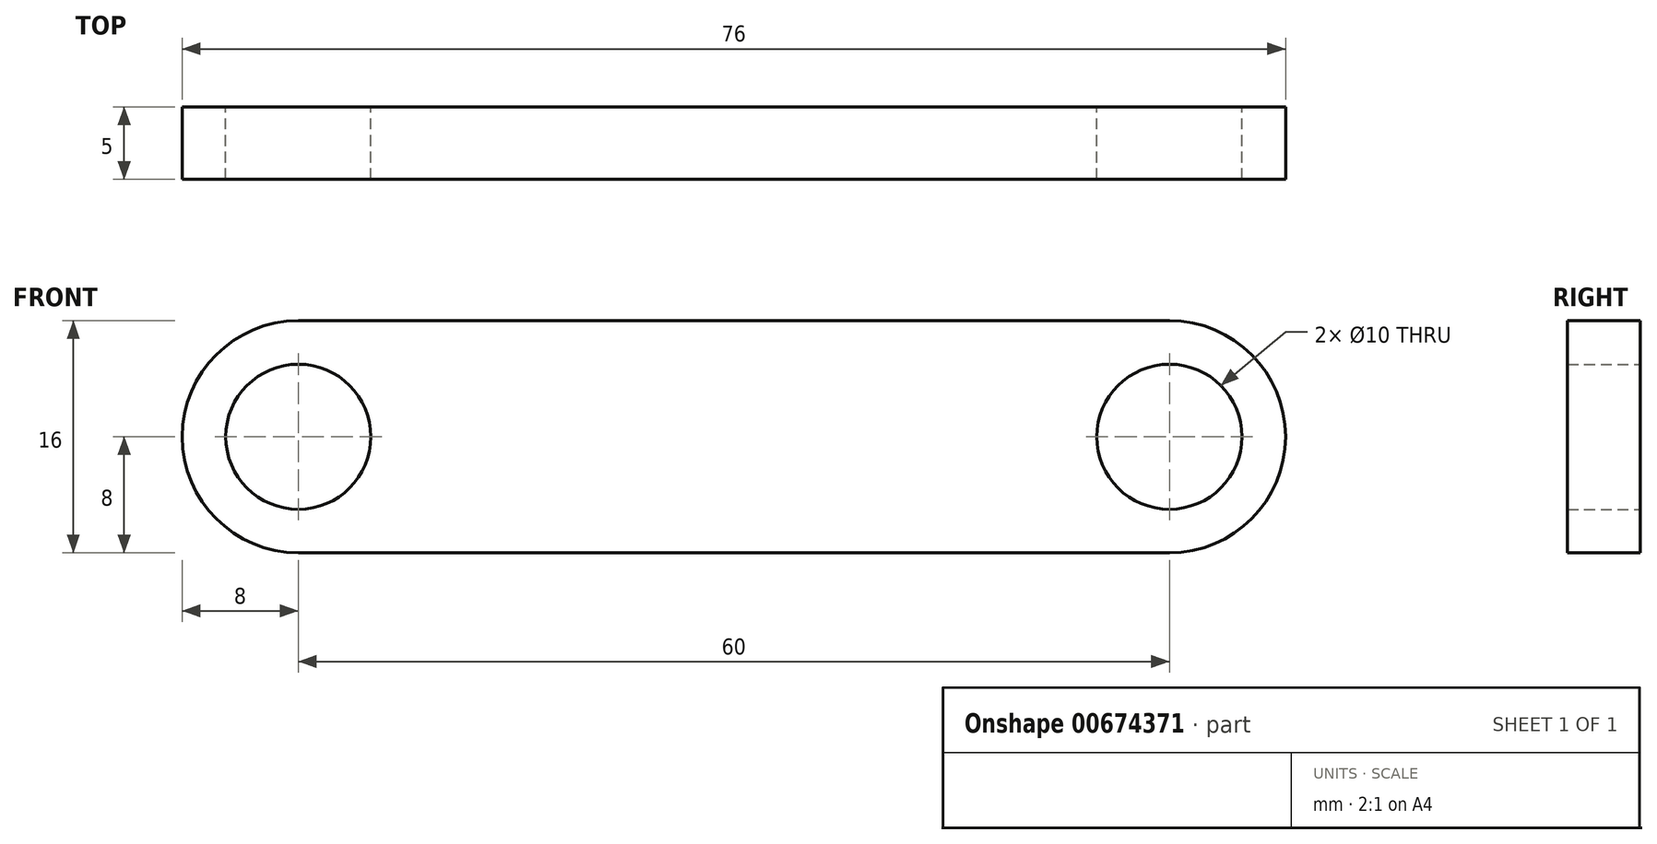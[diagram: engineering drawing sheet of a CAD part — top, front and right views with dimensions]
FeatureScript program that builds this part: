
annotation { "Feature Type Name" : "Feature", "Feature Type Description" : "" }
export const myFeature = defineFeature(function(context is Context, id is Id, definition is map)
    precondition{}
    {
        {
            var Q0;
            Q0=qCreatedBy(makeId("Front.planeOp"),FACE);
            var sketch = newSketch(context, id + "F0", { "sketchPlane" : qUnion([Q0])});
            skLineSegment(sketch, "E0.bottom", {"start": v(30, -8) * mm, "end": v(-30, -8) * mm});
            skLineSegment(sketch, "E0.top", {"start": v(30, 8) * mm, "end": v(-30, 8) * mm});
            skPoint(sketch, "E0.middle", {"position": v(0, 0) * mm});
            skArc(sketch, "E1", {"start": v(-30, 8) * mm, "mid": v(-38, 0) * mm, "end": v(-30, -8) * mm});
            skArc(sketch, "E2", {"start": v(30, -8) * mm, "mid": v(38, 0) * mm, "end": v(30, 8) * mm});
            skCircle(sketch, "E3", {"center": v(-30, 0) * mm, "radius": 5 * mm});
            skCircle(sketch, "E4", {"center": v(30, 0) * mm, "radius": 5 * mm});
            skSolve(sketch);
        }
        {
            var Q0;
            Q0=makeQuery(id+"F0.imprint","IMPRINT",FACE,{"disambiguationData":[TD([[makeQuery(id+"F0.imprint","IMPRINT",EDGE,{"derivedFrom":sQuery(id+"F0.wireOp",EDGE,"E0.bottom")}),-1.0]])]});
            extrude(context, id + "F1", {"entities" : qUnion([Q0]), "endBound" : BoundingType.SYMMETRIC, "depth" : 5 * mm, "offsetDistance" : 25.4 * mm});
        }
    });
